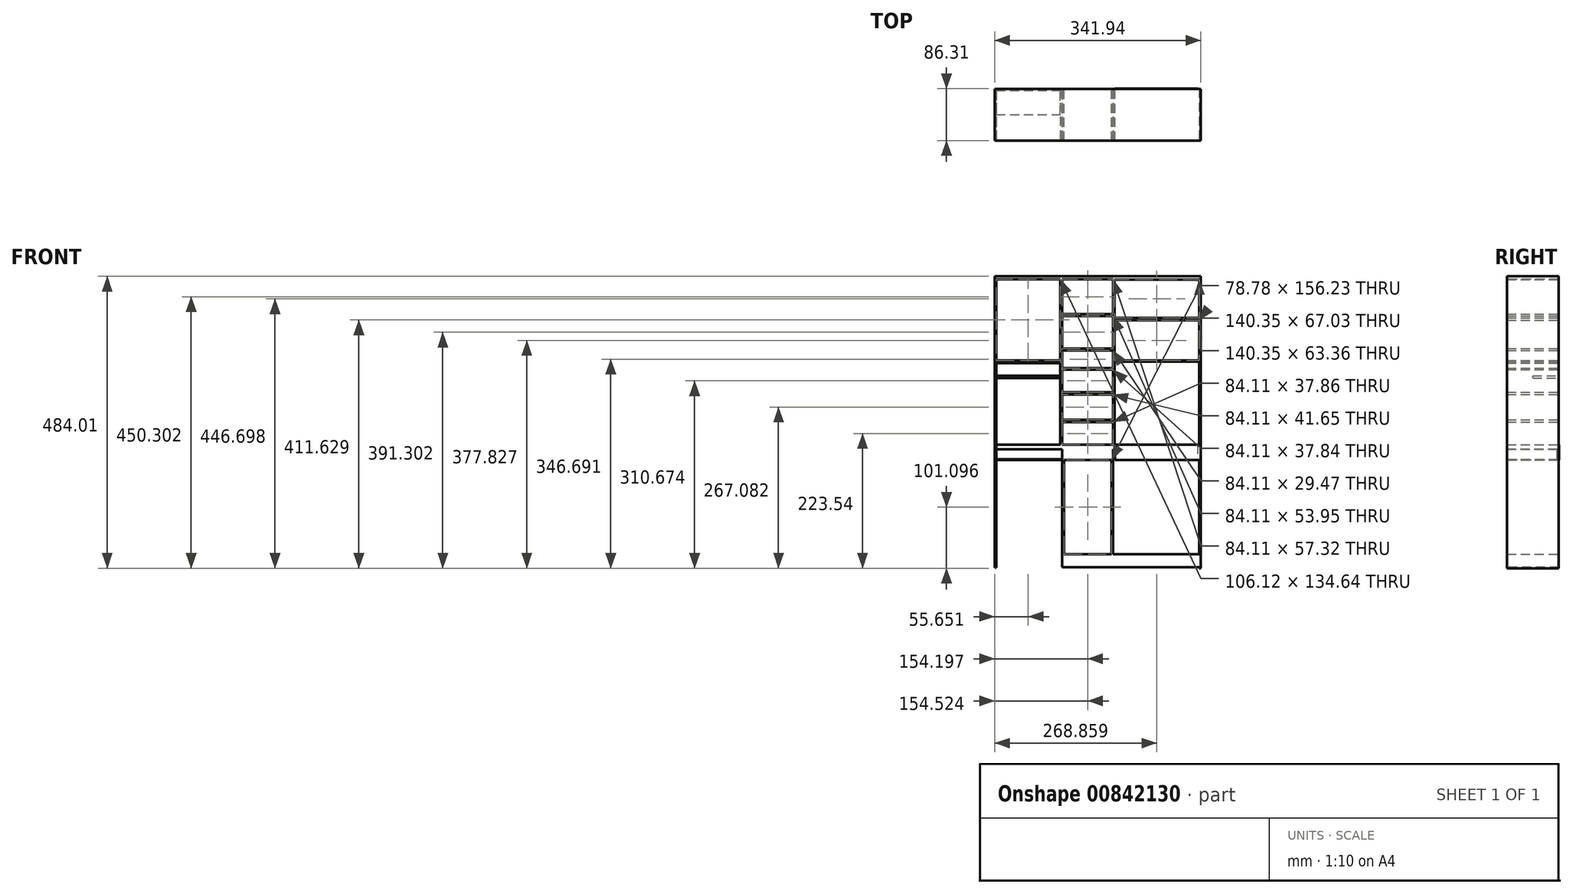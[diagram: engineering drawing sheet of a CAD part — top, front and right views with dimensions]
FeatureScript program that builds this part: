
annotation { "Feature Type Name" : "Feature", "Feature Type Description" : "" }
export const myFeature = defineFeature(function(context is Context, id is Id, definition is map)
    precondition{}
    {
        {
            var Q0;
            Q0=qCreatedBy(makeId("Top.planeOp"),FACE);
            var sketch = newSketch(context, id + "F0", { "sketchPlane" : qUnion([Q0])});
            skLineSegment(sketch, "E0.bottom", {"start": v(-181.1, 86) * mm, "end": v(155.92, 86) * mm});
            skLineSegment(sketch, "E0.top", {"start": v(-181.1, 0) * mm, "end": v(155.92, 0) * mm});
            skLineSegment(sketch, "E0.left", {"start": v(-181.1, 86) * mm, "end": v(-181.1, 0) * mm});
            skLineSegment(sketch, "E0.right", {"start": v(155.92, 86) * mm, "end": v(155.92, 0) * mm});
            skSolve(sketch);
        }
        {
            var Q0;
            Q0 = qSketchRegion(id + "F0", true);
            extrude(context, id + "F1", {"entities" : qUnion([Q0]), "depth" : 7.62 * mm, "offsetDistance" : 25.4 * mm});
        }
        {
            var Q0;
            Q0=makeQuery(id+"F1.opExtrude","CAP_FACE",FACE,{"disambiguationData":[OSD([sQuery(id+"F0.wireOp",EDGE,"E0.bottom"),sQuery(id+"F0.wireOp",EDGE,"E0.top"),sQuery(id+"F0.wireOp",EDGE,"E0.left"),sQuery(id+"F0.wireOp",EDGE,"E0.right")])],"isStart":false});
            var sketch = newSketch(context, id + "F2", { "sketchPlane" : qUnion([Q0])});
            skLineSegment(sketch, "E1.bottom", {"start": v(-75.06, 86) * mm, "end": v(-71.63, 86) * mm});
            skLineSegment(sketch, "E1.top", {"start": v(-75.06, 0) * mm, "end": v(-71.63, 0) * mm});
            skLineSegment(sketch, "E1.left", {"start": v(-75.06, 86) * mm, "end": v(-75.06, 0) * mm});
            skLineSegment(sketch, "E1.right", {"start": v(-71.63, 86) * mm, "end": v(-71.63, 0) * mm});
            skSolve(sketch);
        }
        {
            var Q0;
            Q0 = qSketchRegion(id + "F2", true);
            extrude(context, id + "F3", {"entities" : qUnion([Q0]), "operationType" : NewBodyOperationType.ADD, "depth" : 279.4 * mm, "offsetDistance" : 25.4 * mm});
        }
        {
            var Q0;
            Q0=makeQuery(id+"F3.opExtrude","SWEPT_FACE",FACE,{"disambiguationData":[OSD([sQuery(id+"F2.wireOp",EDGE,"E1.left")])]});
            var sketch = newSketch(context, id + "F4", { "sketchPlane" : qUnion([Q0])});
            skLineSegment(sketch, "E2.bottom", {"start": v(0, 147.32) * mm, "end": v(-86, 147.32) * mm});
            skLineSegment(sketch, "E2.top", {"start": v(0, 142.91) * mm, "end": v(-86, 142.91) * mm});
            skLineSegment(sketch, "E2.left", {"start": v(0, 147.32) * mm, "end": v(0, 142.91) * mm});
            skLineSegment(sketch, "E2.right", {"start": v(-86, 147.32) * mm, "end": v(-86, 142.91) * mm});
            skSolve(sketch);
        }
        {
            var Q0;
            Q0 = qSketchRegion(id + "F4", true);
            extrude(context, id + "F5", {"entities" : qUnion([Q0]), "operationType" : NewBodyOperationType.ADD, "depth" : 108.7 * mm, "offsetDistance" : 25.4 * mm});
        }
        {
            var Q0;
            Q0=makeQuery(id+"F5.boolean.opBoolean","SPLIT",FACE,{"disambiguationData":[TD([makeQuery(id+"F5.opExtrude","SWEPT_FACE",FACE,{"disambiguationData":[OSD([sQuery(id+"F4.wireOp",EDGE,"E2.top")])]})])],"derivedFrom":makeQuery(id+"F3.opExtrude","SWEPT_FACE",FACE,{"disambiguationData":[OSD([sQuery(id+"F2.wireOp",EDGE,"E1.left")])]})});
            var sketch = newSketch(context, id + "F6", { "sketchPlane" : qUnion([Q0])});
            skPoint(sketch, "E3.firstSnap0", {"position": v(-43, 142.91) * mm});
            skLineSegment(sketch, "E3.bottom", {"start": v(-43, 118.16) * mm, "end": v(-86, 118.16) * mm});
            skLineSegment(sketch, "E3.top", {"start": v(-43, 122.35) * mm, "end": v(-86, 122.35) * mm});
            skLineSegment(sketch, "E3.left", {"start": v(-43, 118.16) * mm, "end": v(-43, 122.35) * mm});
            skLineSegment(sketch, "E3.right", {"start": v(-86, 118.16) * mm, "end": v(-86, 122.35) * mm});
            skSolve(sketch);
        }
        {
            var Q0;
            Q0 = qSketchRegion(id + "F6", true);
            extrude(context, id + "F7", {"entities" : qUnion([Q0]), "operationType" : NewBodyOperationType.ADD, "depth" : 108.7 * mm, "offsetDistance" : 25.4 * mm});
        }
        {
            var Q0;
            {var subQ1=sQuery(id+"F2.wireOp",EDGE,"E1.left");Q0=makeQuery(id+"F5.boolean.opBoolean","SPLIT",FACE,{"disambiguationData":[TD([makeQuery(id+"F5.opExtrude","SWEPT_FACE",FACE,{"disambiguationData":[OSD([sQuery(id+"F4.wireOp",EDGE,"E2.bottom")])]})])],"derivedFrom":makeQuery(id+"F3.opExtrude","SWEPT_FACE",FACE,{"disambiguationData":[OSD([subQ1])]})});}
            var sketch = newSketch(context, id + "F8", { "sketchPlane" : qUnion([Q0])});
            skLineSegment(sketch, "E4.bottom", {"start": v(-86, 287.02) * mm, "end": v(0, 287.02) * mm});
            skLineSegment(sketch, "E4.top", {"start": v(-86, 281.96) * mm, "end": v(0, 281.96) * mm});
            skLineSegment(sketch, "E4.left", {"start": v(-86, 287.02) * mm, "end": v(-86, 281.96) * mm});
            skLineSegment(sketch, "E4.right", {"start": v(0, 287.02) * mm, "end": v(0, 281.96) * mm});
            skSolve(sketch);
        }
        {
            var Q0;
            Q0=makeQuery(id+"F8.imprint","IMPRINT",FACE,{"disambiguationData":[TD([[makeQuery(id+"F8.imprint","IMPRINT",EDGE,{"derivedFrom":sQuery(id+"F8.wireOp",EDGE,"E4.bottom")}),-1.0]])]});
            extrude(context, id + "F9", {"entities" : qUnion([Q0]), "operationType" : NewBodyOperationType.ADD, "depth" : 108.7 * mm, "offsetDistance" : 25.4 * mm});
        }
        {
            var Q0;
            Q0=makeQuery(id+"F9.opExtrude","SWEPT_FACE",FACE,{"disambiguationData":[OSD([sQuery(id+"F8.wireOp",EDGE,"E4.top")])]});
            var sketch = newSketch(context, id + "F10", { "sketchPlane" : qUnion([Q0])});
            skLineSegment(sketch, "E5.bottom", {"start": v(-183.77, -86) * mm, "end": v(-181.18, -86) * mm});
            skLineSegment(sketch, "E5.top", {"start": v(-183.77, 0) * mm, "end": v(-181.18, 0) * mm});
            skLineSegment(sketch, "E5.left", {"start": v(-183.77, -86) * mm, "end": v(-183.77, 0) * mm});
            skLineSegment(sketch, "E5.right", {"start": v(-181.18, -86) * mm, "end": v(-181.18, 0) * mm});
            skSolve(sketch);
        }
        {
            var Q0;
            Q0 = qSketchRegion(id + "F10", true);
            extrude(context, id + "F11", {"entities" : qUnion([Q0]), "operationType" : NewBodyOperationType.ADD, "depth" : 282.7 * mm, "offsetDistance" : 25.4 * mm});
        }
        {
            var Q0;
            {var subQ0=sQuery(id+"F0.wireOp",EDGE,"E0.top");var subQ1=sQuery(id+"F0.wireOp",EDGE,"E0.right");var subQ2=sQuery(id+"F0.wireOp",EDGE,"E0.bottom");Q0=makeQuery(id+"F3.boolean.opBoolean","SPLIT",FACE,{"disambiguationData":[TD([makeQuery(id+"F1.opExtrude","SWEPT_FACE",FACE,{"disambiguationData":[OSD([subQ1])]})])],"derivedFrom":makeQuery(id+"F1.opExtrude","CAP_FACE",FACE,{"disambiguationData":[OSD([subQ2,subQ0,sQuery(id+"F0.wireOp",EDGE,"E0.left"),subQ1])],"isStart":false})});}
            var sketch = newSketch(context, id + "F12", { "sketchPlane" : qUnion([Q0])});
            skLineSegment(sketch, "E6.bottom", {"start": v(-71.63, 86) * mm, "end": v(12.9, 86) * mm});
            skLineSegment(sketch, "E6.top", {"start": v(-71.63, 0) * mm, "end": v(12.9, 0) * mm});
            skLineSegment(sketch, "E6.left", {"start": v(-71.63, 86) * mm, "end": v(-71.63, 0) * mm});
            skLineSegment(sketch, "E6.right", {"start": v(12.9, 86) * mm, "end": v(12.9, 0) * mm});
            skSolve(sketch);
        }
        {
            var Q0;
            Q0 = qSketchRegion(id + "F12", true);
            extrude(context, id + "F13", {"entities" : qUnion([Q0]), "operationType" : NewBodyOperationType.ADD, "oppositeDirection" : true, "depth" : 25.4 * mm, "offsetDistance" : 25.4 * mm});
        }
        {
            var Q0;
            {var subQ0=sQuery(id+"F0.wireOp",EDGE,"E0.top");var subQ1=sQuery(id+"F0.wireOp",EDGE,"E0.right");var subQ2=sQuery(id+"F0.wireOp",EDGE,"E0.bottom");Q0=makeQuery(id+"F3.boolean.opBoolean","SPLIT",FACE,{"disambiguationData":[TD([makeQuery(id+"F1.opExtrude","SWEPT_FACE",FACE,{"disambiguationData":[OSD([subQ1])]})])],"derivedFrom":makeQuery(id+"F1.opExtrude","CAP_FACE",FACE,{"disambiguationData":[OSD([subQ2,subQ0,sQuery(id+"F0.wireOp",EDGE,"E0.left"),subQ1])],"isStart":false})});}
            var sketch = newSketch(context, id + "F14", { "sketchPlane" : qUnion([Q0])});
            skLineSegment(sketch, "E7.bottom", {"start": v(14.91, 0) * mm, "end": v(12.48, 0) * mm});
            skLineSegment(sketch, "E7.top", {"start": v(14.91, 86) * mm, "end": v(12.48, 86) * mm});
            skLineSegment(sketch, "E7.left", {"start": v(14.91, 0) * mm, "end": v(14.91, 86) * mm});
            skLineSegment(sketch, "E7.right", {"start": v(12.48, 0) * mm, "end": v(12.48, 86) * mm});
            skSolve(sketch);
        }
        {
            var Q0;
            Q0 = qSketchRegion(id + "F14", true);
            extrude(context, id + "F15", {"entities" : qUnion([Q0]), "operationType" : NewBodyOperationType.ADD, "depth" : 279.4 * mm, "offsetDistance" : 25.4 * mm});
        }
        {
            var Q0;
            Q0=makeQuery(id+"F3.opExtrude","SWEPT_FACE",FACE,{"disambiguationData":[OSD([sQuery(id+"F2.wireOp",EDGE,"E1.right")])]});
            var sketch = newSketch(context, id + "F16", { "sketchPlane" : qUnion([Q0])});
            skLineSegment(sketch, "E8.bottom", {"start": v(0, 287.02) * mm, "end": v(86, 287.02) * mm});
            skLineSegment(sketch, "E8.top", {"start": v(0, 281.97) * mm, "end": v(86, 281.97) * mm});
            skLineSegment(sketch, "E8.left", {"start": v(0, 287.02) * mm, "end": v(0, 281.97) * mm});
            skLineSegment(sketch, "E8.right", {"start": v(86, 287.02) * mm, "end": v(86, 281.97) * mm});
            skSolve(sketch);
        }
        {
            var Q0;
            Q0 = qSketchRegion(id + "F16", true);
            extrude(context, id + "F17", {"entities" : qUnion([Q0]), "operationType" : NewBodyOperationType.ADD, "depth" : 84.84 * mm, "offsetDistance" : 25.4 * mm});
        }
        {
            var Q0;
            Q0=makeQuery(id+"F3.opExtrude","SWEPT_FACE",FACE,{"disambiguationData":[OSD([sQuery(id+"F2.wireOp",EDGE,"E1.right")])]});
            var sketch = newSketch(context, id + "F18", { "sketchPlane" : qUnion([Q0])});
            skLineSegment(sketch, "E9.bottom", {"start": v(0, 164.43) * mm, "end": v(86, 164.43) * mm});
            skLineSegment(sketch, "E9.top", {"start": v(0, 167.33) * mm, "end": v(86, 167.33) * mm});
            skLineSegment(sketch, "E9.left", {"start": v(0, 164.43) * mm, "end": v(0, 167.33) * mm});
            skLineSegment(sketch, "E9.right", {"start": v(86, 164.43) * mm, "end": v(86, 167.33) * mm});
            skSolve(sketch);
        }
        {
            var Q0;
            Q0 = qSketchRegion(id + "F18", true);
            extrude(context, id + "F19", {"entities" : qUnion([Q0]), "operationType" : NewBodyOperationType.ADD, "depth" : 84.84 * mm, "offsetDistance" : 25.4 * mm});
        }
        {
            var Q0;
            Q0=makeQuery(id+"F19.boolean.opBoolean","SPLIT",FACE,{"disambiguationData":[TD([makeQuery(id+"F17.opExtrude","SWEPT_FACE",FACE,{"disambiguationData":[OSD([sQuery(id+"F16.wireOp",EDGE,"E8.top")])]})])],"derivedFrom":makeQuery(id+"F3.opExtrude","SWEPT_FACE",FACE,{"disambiguationData":[OSD([sQuery(id+"F2.wireOp",EDGE,"E1.right")])]})});
            var sketch = newSketch(context, id + "F20", { "sketchPlane" : qUnion([Q0])});
            skLineSegment(sketch, "E10.bottom", {"start": v(0, 224.65) * mm, "end": v(86, 224.65) * mm});
            skLineSegment(sketch, "E10.top", {"start": v(0, 221.29) * mm, "end": v(86, 221.29) * mm});
            skLineSegment(sketch, "E10.left", {"start": v(0, 224.65) * mm, "end": v(0, 221.29) * mm});
            skLineSegment(sketch, "E10.right", {"start": v(86, 224.65) * mm, "end": v(86, 221.29) * mm});
            skSolve(sketch);
        }
        {
            var Q0;
            Q0 = qSketchRegion(id + "F20", true);
            extrude(context, id + "F21", {"entities" : qUnion([Q0]), "operationType" : NewBodyOperationType.ADD, "depth" : 85.1 * mm, "offsetDistance" : 25.4 * mm});
        }
        {
            var Q0;
            Q0=makeQuery(id+"F19.boolean.opBoolean","SPLIT",FACE,{"disambiguationData":[TD([makeQuery(id+"F19.opExtrude","SWEPT_FACE",FACE,{"disambiguationData":[OSD([sQuery(id+"F18.wireOp",EDGE,"E9.bottom")])]})])],"derivedFrom":makeQuery(id+"F3.opExtrude","SWEPT_FACE",FACE,{"disambiguationData":[OSD([sQuery(id+"F2.wireOp",EDGE,"E1.right")])]})});
            var sketch = newSketch(context, id + "F22", { "sketchPlane" : qUnion([Q0])});
            skLineSegment(sketch, "E11.bottom", {"start": v(0, 132.6) * mm, "end": v(86, 132.6) * mm});
            skLineSegment(sketch, "E11.top", {"start": v(0, 134.97) * mm, "end": v(86, 134.97) * mm});
            skLineSegment(sketch, "E11.left", {"start": v(0, 132.6) * mm, "end": v(0, 134.97) * mm});
            skLineSegment(sketch, "E11.right", {"start": v(86, 132.6) * mm, "end": v(86, 134.97) * mm});
            skSolve(sketch);
        }
        {
            var Q0;
            Q0 = qSketchRegion(id + "F22", true);
            extrude(context, id + "F23", {"entities" : qUnion([Q0]), "operationType" : NewBodyOperationType.ADD, "depth" : 85.1 * mm, "offsetDistance" : 25.4 * mm});
        }
        {
            var Q0;
            Q0=makeQuery(id+"F23.boolean.opBoolean","SPLIT",FACE,{"disambiguationData":[TD([makeQuery(id+"F23.opExtrude","SWEPT_FACE",FACE,{"disambiguationData":[OSD([sQuery(id+"F22.wireOp",EDGE,"E11.bottom")])]})])],"derivedFrom":makeQuery(id+"F19.boolean.opBoolean","SPLIT",FACE,{"disambiguationData":[TD([makeQuery(id+"F19.opExtrude","SWEPT_FACE",FACE,{"disambiguationData":[OSD([sQuery(id+"F18.wireOp",EDGE,"E9.bottom")])]})])],"derivedFrom":makeQuery(id+"F3.opExtrude","SWEPT_FACE",FACE,{"disambiguationData":[OSD([sQuery(id+"F2.wireOp",EDGE,"E1.right")])]})})});
            var sketch = newSketch(context, id + "F24", { "sketchPlane" : qUnion([Q0])});
            skLineSegment(sketch, "E12.bottom", {"start": v(0, 94.76) * mm, "end": v(86, 94.76) * mm});
            skLineSegment(sketch, "E12.top", {"start": v(0, 90.92) * mm, "end": v(86, 90.92) * mm});
            skLineSegment(sketch, "E12.left", {"start": v(0, 94.76) * mm, "end": v(0, 90.92) * mm});
            skLineSegment(sketch, "E12.right", {"start": v(86, 94.76) * mm, "end": v(86, 90.92) * mm});
            skSolve(sketch);
        }
        {
            var Q0;
            Q0 = qSketchRegion(id + "F24", true);
            extrude(context, id + "F25", {"entities" : qUnion([Q0]), "operationType" : NewBodyOperationType.ADD, "depth" : 85.1 * mm, "offsetDistance" : 25.4 * mm});
        }
        {
            var Q0;
            Q0=makeQuery(id+"F25.boolean.opBoolean","SPLIT",FACE,{"disambiguationData":[TD([makeQuery(id+"F25.opExtrude","SWEPT_FACE",FACE,{"disambiguationData":[OSD([sQuery(id+"F24.wireOp",EDGE,"E12.top")])]})])],"derivedFrom":makeQuery(id+"F23.boolean.opBoolean","SPLIT",FACE,{"disambiguationData":[TD([makeQuery(id+"F23.opExtrude","SWEPT_FACE",FACE,{"disambiguationData":[OSD([sQuery(id+"F22.wireOp",EDGE,"E11.bottom")])]})])],"derivedFrom":makeQuery(id+"F19.boolean.opBoolean","SPLIT",FACE,{"disambiguationData":[TD([makeQuery(id+"F19.opExtrude","SWEPT_FACE",FACE,{"disambiguationData":[OSD([sQuery(id+"F18.wireOp",EDGE,"E9.bottom")])]})])],"derivedFrom":makeQuery(id+"F3.opExtrude","SWEPT_FACE",FACE,{"disambiguationData":[OSD([sQuery(id+"F2.wireOp",EDGE,"E1.right")])]})})})});
            var sketch = newSketch(context, id + "F26", { "sketchPlane" : qUnion([Q0])});
            skLineSegment(sketch, "E13.bottom", {"start": v(0, 49.27) * mm, "end": v(86, 49.27) * mm});
            skLineSegment(sketch, "E13.top", {"start": v(0, 45.48) * mm, "end": v(86, 45.48) * mm});
            skLineSegment(sketch, "E13.left", {"start": v(0, 49.27) * mm, "end": v(0, 45.48) * mm});
            skLineSegment(sketch, "E13.right", {"start": v(86, 49.27) * mm, "end": v(86, 45.48) * mm});
            skSolve(sketch);
        }
        {
            var Q0;
            Q0 = qSketchRegion(id + "F26", true);
            extrude(context, id + "F27", {"entities" : qUnion([Q0]), "operationType" : NewBodyOperationType.ADD, "depth" : 85.1 * mm, "offsetDistance" : 25.4 * mm});
        }
        {
            var Q0;
            {var subQ1=sQuery(id+"F0.wireOp",EDGE,"E0.bottom");var subQ3=sQuery(id+"F0.wireOp",EDGE,"E0.right");var subQ4=makeQuery(id+"F1.opExtrude","SWEPT_FACE",FACE,{"disambiguationData":[OSD([subQ3])]});var subQ5=sQuery(id+"F0.wireOp",EDGE,"E0.top");Q0=makeQuery(id+"F15.boolean.opBoolean","SPLIT",FACE,{"disambiguationData":[TD([subQ4])],"derivedFrom":makeQuery(id+"F3.boolean.opBoolean","SPLIT",FACE,{"disambiguationData":[TD([subQ4])],"derivedFrom":makeQuery(id+"F1.opExtrude","CAP_FACE",FACE,{"disambiguationData":[OSD([subQ1,subQ5,sQuery(id+"F0.wireOp",EDGE,"E0.left"),subQ3])],"isStart":false})})});}
            var sketch = newSketch(context, id + "F28", { "sketchPlane" : qUnion([Q0])});
            skSolve(sketch);
        }
        {
            var Q0;
            {var subQ0=sQuery(id+"F0.wireOp",EDGE,"E0.right");Q0=makeQuery(id+"F28.imprint","IMPRINT",FACE,{"disambiguationData":[TD([[makeQuery(id+"F28.imprint","IMPRINT",EDGE,{"derivedFrom":makeQuery(id+"F1.opExtrude","CAP_EDGE",EDGE,{"disambiguationData":[OSD([subQ0])],"isStart":false})}),-1.0]])]});}
            var sketch = newSketch(context, id + "F29", { "sketchPlane" : qUnion([Q0])});
            skLineSegment(sketch, "E14.bottom", {"start": v(15.66, 0) * mm, "end": v(153.22, 0) * mm});
            skLineSegment(sketch, "E14.top", {"start": v(15.66, 86.3) * mm, "end": v(153.22, 86.3) * mm});
            skLineSegment(sketch, "E14.left", {"start": v(15.66, 0) * mm, "end": v(15.66, 86.3) * mm});
            skLineSegment(sketch, "E14.right", {"start": v(153.22, 0) * mm, "end": v(153.22, 86.3) * mm});
            skSolve(sketch);
        }
        {
            var Q0;
            Q0 = qSketchRegion(id + "F29", true);
            extrude(context, id + "F30", {"entities" : qUnion([Q0]), "operationType" : NewBodyOperationType.ADD, "oppositeDirection" : true, "depth" : 25.4 * mm, "offsetDistance" : 25.4 * mm});
        }
        {
            var Q0;
            Q0=makeQuery(id+"F15.opExtrude","SWEPT_FACE",FACE,{"disambiguationData":[OSD([sQuery(id+"F14.wireOp",EDGE,"E7.left")])]});
            var sketch = newSketch(context, id + "F31", { "sketchPlane" : qUnion([Q0])});
            skLineSegment(sketch, "E15.bottom", {"start": v(0, 147.32) * mm, "end": v(86, 147.32) * mm});
            skLineSegment(sketch, "E15.top", {"start": v(0, 145.59) * mm, "end": v(86, 145.59) * mm});
            skLineSegment(sketch, "E15.left", {"start": v(0, 147.32) * mm, "end": v(0, 145.59) * mm});
            skLineSegment(sketch, "E15.right", {"start": v(86, 147.32) * mm, "end": v(86, 145.59) * mm});
            skSolve(sketch);
        }
        {
            var Q0;
            Q0 = qSketchRegion(id + "F31", true);
            extrude(context, id + "F32", {"entities" : qUnion([Q0]), "operationType" : NewBodyOperationType.ADD, "depth" : 143.26 * mm, "offsetDistance" : 25.4 * mm});
        }
        {
            var Q0;
            {var subQ2=sQuery(id+"F14.wireOp",EDGE,"E7.left");Q0=makeQuery(id+"F32.boolean.opBoolean","SPLIT",FACE,{"disambiguationData":[TD([makeQuery(id+"F9.opExtrude","SWEPT_FACE",FACE,{"disambiguationData":[OSD([sQuery(id+"F8.wireOp",EDGE,"E4.bottom")])]})])],"derivedFrom":makeQuery(id+"F15.opExtrude","SWEPT_FACE",FACE,{"disambiguationData":[OSD([subQ2])]})});}
            var sketch = newSketch(context, id + "F33", { "sketchPlane" : qUnion([Q0])});
            skLineSegment(sketch, "E16.bottom", {"start": v(0, 287.02) * mm, "end": v(86, 287.02) * mm});
            skLineSegment(sketch, "E16.top", {"start": v(0, 281.39) * mm, "end": v(86, 281.39) * mm});
            skLineSegment(sketch, "E16.left", {"start": v(0, 287.02) * mm, "end": v(0, 281.39) * mm});
            skLineSegment(sketch, "E16.right", {"start": v(86, 287.02) * mm, "end": v(86, 281.39) * mm});
            skSolve(sketch);
        }
        {
            var Q0;
            Q0=makeQuery(id+"F33.imprint","IMPRINT",FACE,{"disambiguationData":[TD([[makeQuery(id+"F33.imprint","IMPRINT",EDGE,{"derivedFrom":sQuery(id+"F33.wireOp",EDGE,"E16.bottom")}),-1.0]])]});
            extrude(context, id + "F34", {"entities" : qUnion([Q0]), "operationType" : NewBodyOperationType.ADD, "depth" : 143.26 * mm, "offsetDistance" : 25.4 * mm});
        }
        {
            var Q0;
            Q0=makeQuery(id+"F34.opExtrude","SWEPT_FACE",FACE,{"disambiguationData":[OSD([sQuery(id+"F33.wireOp",EDGE,"E16.top")])]});
            var sketch = newSketch(context, id + "F35", { "sketchPlane" : qUnion([Q0])});
            skLineSegment(sketch, "E17.bottom", {"start": v(158.17, 0) * mm, "end": v(155.27, 0) * mm});
            skLineSegment(sketch, "E17.top", {"start": v(158.17, -86) * mm, "end": v(155.27, -86) * mm});
            skLineSegment(sketch, "E17.left", {"start": v(158.17, 0) * mm, "end": v(158.17, -86) * mm});
            skLineSegment(sketch, "E17.right", {"start": v(155.27, 0) * mm, "end": v(155.27, -86) * mm});
            skSolve(sketch);
        }
        {
            var Q0;
            Q0 = qSketchRegion(id + "F35", true);
            extrude(context, id + "F36", {"entities" : qUnion([Q0]), "operationType" : NewBodyOperationType.ADD, "depth" : 300.58 * mm, "offsetDistance" : 25.4 * mm});
        }
        {
            var Q0;
            {var subQ2=sQuery(id+"F14.wireOp",EDGE,"E7.left");Q0=makeQuery(id+"F32.boolean.opBoolean","SPLIT",FACE,{"disambiguationData":[TD([makeQuery(id+"F9.opExtrude","SWEPT_FACE",FACE,{"disambiguationData":[OSD([sQuery(id+"F8.wireOp",EDGE,"E4.bottom")])]})])],"derivedFrom":makeQuery(id+"F15.opExtrude","SWEPT_FACE",FACE,{"disambiguationData":[OSD([subQ2])]})});}
            var sketch = newSketch(context, id + "F37", { "sketchPlane" : qUnion([Q0])});
            skLineSegment(sketch, "E18.bottom", {"start": v(0, 214.35) * mm, "end": v(86, 214.35) * mm});
            skLineSegment(sketch, "E18.top", {"start": v(0, 218.03) * mm, "end": v(86, 218.03) * mm});
            skLineSegment(sketch, "E18.left", {"start": v(0, 214.35) * mm, "end": v(0, 218.03) * mm});
            skLineSegment(sketch, "E18.right", {"start": v(86, 214.35) * mm, "end": v(86, 218.03) * mm});
            skSolve(sketch);
        }
        {
            var Q0;
            Q0 = qSketchRegion(id + "F37", true);
            extrude(context, id + "F38", {"entities" : qUnion([Q0]), "operationType" : NewBodyOperationType.ADD, "depth" : 141.73 * mm, "offsetDistance" : 25.4 * mm});
        }
        {
            var Q0;
            {var subQ0=sQuery(id+"F0.wireOp",EDGE,"E0.bottom");var subQ1=sQuery(id+"F0.wireOp",EDGE,"E0.top");var subQ2=sQuery(id+"F0.wireOp",EDGE,"E0.left");Q0=makeQuery(id+"F13.boolean.opBoolean","SPLIT",FACE,{"disambiguationData":[TD([makeQuery(id+"F1.opExtrude","SWEPT_FACE",FACE,{"disambiguationData":[OSD([subQ2])]})])],"derivedFrom":makeQuery(id+"F1.opExtrude","CAP_FACE",FACE,{"disambiguationData":[OSD([subQ0,subQ1,subQ2,sQuery(id+"F0.wireOp",EDGE,"E0.right")])],"isStart":true})});}
            var sketch = newSketch(context, id + "F39", { "sketchPlane" : qUnion([Q0])});
            skLineSegment(sketch, "E19.bottom", {"start": v(-181.1, -86) * mm, "end": v(-71.63, -86) * mm});
            skLineSegment(sketch, "E19.top", {"start": v(-181.1, -83.2) * mm, "end": v(-71.63, -83.2) * mm});
            skLineSegment(sketch, "E19.left", {"start": v(-181.1, -86) * mm, "end": v(-181.1, -83.2) * mm});
            skLineSegment(sketch, "E19.right", {"start": v(-71.63, -86) * mm, "end": v(-71.63, -83.2) * mm});
            skSolve(sketch);
        }
        {
            var Q0;
            Q0 = qSketchRegion(id + "F39", true);
            extrude(context, id + "F40", {"entities" : qUnion([Q0]), "operationType" : NewBodyOperationType.ADD, "depth" : 17.78 * mm, "offsetDistance" : 25.4 * mm});
        }
        {
            var Q0;
            Q0=makeQuery(id+"F11.opExtrude","CAP_FACE",FACE,{"disambiguationData":[OSD([sQuery(id+"F10.wireOp",EDGE,"E5.bottom"),sQuery(id+"F10.wireOp",EDGE,"E5.top"),sQuery(id+"F10.wireOp",EDGE,"E5.left"),sQuery(id+"F10.wireOp",EDGE,"E5.right")])],"isStart":false});
            var sketch = newSketch(context, id + "F41", { "sketchPlane" : qUnion([Q0])});
            skLineSegment(sketch, "E20.bottom", {"start": v(-181.18, -86) * mm, "end": v(-183.77, -86) * mm});
            skLineSegment(sketch, "E20.top", {"start": v(-181.18, -83.2) * mm, "end": v(-183.77, -83.2) * mm});
            skLineSegment(sketch, "E20.left", {"start": v(-181.18, -86) * mm, "end": v(-181.18, -83.2) * mm});
            skLineSegment(sketch, "E20.right", {"start": v(-183.77, -86) * mm, "end": v(-183.77, -83.2) * mm});
            skSolve(sketch);
        }
        {
            var Q0;
            Q0 = qSketchRegion(id + "F41", true);
            extrude(context, id + "F42", {"entities" : qUnion([Q0]), "operationType" : NewBodyOperationType.ADD, "depth" : 17.07 * mm, "offsetDistance" : 25.4 * mm});
        }
        {
            var Q0;
            Q0=makeQuery(id+"F42.opExtrude","SWEPT_FACE",FACE,{"disambiguationData":[OSD([sQuery(id+"F41.wireOp",EDGE,"E20.top")])]});
            extrude(context, id + "F43", {"entities" : qUnion([Q0]), "operationType" : NewBodyOperationType.ADD, "depth" : 83.16 * mm, "offsetDistance" : 25.4 * mm});
        }
        {
            var Q0;
            Q0=makeQuery(id+"F40.opExtrude","SWEPT_FACE",FACE,{"disambiguationData":[OSD([sQuery(id+"F39.wireOp",EDGE,"E19.top")])]});
            var sketch = newSketch(context, id + "F44", { "sketchPlane" : qUnion([Q0])});
            skLineSegment(sketch, "E21.bottom", {"start": v(-71.63, -16.3) * mm, "end": v(-181.1, -16.3) * mm});
            skLineSegment(sketch, "E21.top", {"start": v(-71.63, -17.78) * mm, "end": v(-181.1, -17.78) * mm});
            skLineSegment(sketch, "E21.left", {"start": v(-71.63, -16.3) * mm, "end": v(-71.63, -17.78) * mm});
            skLineSegment(sketch, "E21.right", {"start": v(-181.1, -16.3) * mm, "end": v(-181.1, -17.78) * mm});
            skSolve(sketch);
        }
        {
            var Q0;
            Q0 = qSketchRegion(id + "F44", true);
            extrude(context, id + "F45", {"entities" : qUnion([Q0]), "operationType" : NewBodyOperationType.ADD, "depth" : 83.06 * mm, "offsetDistance" : 25.4 * mm});
        }
        {
            var Q0;
            {var subQ0=sQuery(id+"F41.wireOp",EDGE,"E20.top");Q0=makeQuery(id+"F43.boolean.opBoolean","MERGE",FACE,{"derivedFrom":[makeQuery(id+"F42.opExtrude","CAP_FACE",FACE,{"disambiguationData":[OSD([sQuery(id+"F41.wireOp",EDGE,"E20.bottom"),subQ0,sQuery(id+"F41.wireOp",EDGE,"E20.left"),sQuery(id+"F41.wireOp",EDGE,"E20.right")])],"isStart":false}),makeQuery(id+"F43.opExtrude","SWEPT_FACE",FACE,{"disambiguationData":[OSD([subQ0]),TDD([makeQuery(id+"F42.opExtrude","CAP_EDGE",EDGE,{"disambiguationData":[OSD([subQ0])],"isStart":false})])]})]});}
            extrude(context, id + "F46", {"entities" : qUnion([Q0]), "operationType" : NewBodyOperationType.ADD, "depth" : 177.8 * mm, "offsetDistance" : 25.4 * mm});
        }
        {
            var Q0;
            Q0=makeQuery(id+"F45.boolean.opBoolean","MERGE",FACE,{"derivedFrom":[makeQuery(id+"F40.boolean.opBoolean","MERGE",FACE,{"derivedFrom":[makeQuery(id+"F13.opExtrude","CAP_FACE",FACE,{"disambiguationData":[OSD([sQuery(id+"F12.wireOp",EDGE,"E6.bottom"),sQuery(id+"F12.wireOp",EDGE,"E6.top"),sQuery(id+"F12.wireOp",EDGE,"E6.left"),sQuery(id+"F12.wireOp",EDGE,"E6.right")])],"isStart":false}),makeQuery(id+"F40.opExtrude","CAP_FACE",FACE,{"disambiguationData":[OSD([sQuery(id+"F39.wireOp",EDGE,"E19.bottom"),sQuery(id+"F39.wireOp",EDGE,"E19.top"),sQuery(id+"F39.wireOp",EDGE,"E19.left"),sQuery(id+"F39.wireOp",EDGE,"E19.right")])],"isStart":false})]}),makeQuery(id+"F45.opExtrude","SWEPT_FACE",FACE,{"disambiguationData":[OSD([sQuery(id+"F44.wireOp",EDGE,"E21.top")])]})]});
            var sketch = newSketch(context, id + "F47", { "sketchPlane" : qUnion([Q0])});
            skLineSegment(sketch, "E22.bottom", {"start": v(-71.63, 0) * mm, "end": v(-68.64, 0) * mm});
            skLineSegment(sketch, "E22.top", {"start": v(-71.63, -86) * mm, "end": v(-68.64, -86) * mm});
            skLineSegment(sketch, "E22.left", {"start": v(-71.63, 0) * mm, "end": v(-71.63, -86) * mm});
            skLineSegment(sketch, "E22.right", {"start": v(-68.64, 0) * mm, "end": v(-68.64, -86) * mm});
            skSolve(sketch);
        }
        {
            var Q0;
            Q0 = qSketchRegion(id + "F47", true);
            extrude(context, id + "F48", {"entities" : qUnion([Q0]), "operationType" : NewBodyOperationType.ADD, "depth" : 177.8 * mm, "offsetDistance" : 25.4 * mm});
        }
        {
            var Q0;
            {var subQ0=sQuery(id+"F12.wireOp",EDGE,"E6.right");var subQ2=sQuery(id+"F12.wireOp",EDGE,"E6.top");var subQ3=sQuery(id+"F12.wireOp",EDGE,"E6.bottom");var subQ4=sQuery(id+"F39.wireOp",EDGE,"E19.bottom");Q0=makeQuery(id+"F48.boolean.opBoolean","SPLIT",FACE,{"disambiguationData":[TD([makeQuery(id+"F1.opExtrude","SWEPT_FACE",FACE,{"disambiguationData":[OSD([sQuery(id+"F0.wireOp",EDGE,"E0.top")])]})])],"derivedFrom":makeQuery(id+"F45.boolean.opBoolean","MERGE",FACE,{"derivedFrom":[makeQuery(id+"F40.boolean.opBoolean","MERGE",FACE,{"derivedFrom":[makeQuery(id+"F13.opExtrude","CAP_FACE",FACE,{"disambiguationData":[OSD([subQ3,subQ2,sQuery(id+"F12.wireOp",EDGE,"E6.left"),subQ0])],"isStart":false}),makeQuery(id+"F40.opExtrude","CAP_FACE",FACE,{"disambiguationData":[OSD([subQ4,sQuery(id+"F39.wireOp",EDGE,"E19.top"),sQuery(id+"F39.wireOp",EDGE,"E19.left"),sQuery(id+"F39.wireOp",EDGE,"E19.right")])],"isStart":false})]}),makeQuery(id+"F45.opExtrude","SWEPT_FACE",FACE,{"disambiguationData":[OSD([sQuery(id+"F44.wireOp",EDGE,"E21.top")])]})]})});}
            var sketch = newSketch(context, id + "F49", { "sketchPlane" : qUnion([Q0])});
            skLineSegment(sketch, "E23.bottom", {"start": v(12.9, 0) * mm, "end": v(10.14, 0) * mm});
            skLineSegment(sketch, "E23.top", {"start": v(12.9, -86) * mm, "end": v(10.14, -86) * mm});
            skLineSegment(sketch, "E23.left", {"start": v(12.9, 0) * mm, "end": v(12.9, -86) * mm});
            skLineSegment(sketch, "E23.right", {"start": v(10.14, 0) * mm, "end": v(10.14, -86) * mm});
            skSolve(sketch);
        }
        {
            var Q0;
            Q0 = qSketchRegion(id + "F49", true);
            extrude(context, id + "F50", {"entities" : qUnion([Q0]), "operationType" : NewBodyOperationType.ADD, "depth" : 177.8 * mm, "offsetDistance" : 25.4 * mm});
        }
        {
            var Q0;
            {var subQ4=sQuery(id+"F0.wireOp",EDGE,"E0.right");var subQ5=makeQuery(id+"F1.opExtrude","SWEPT_FACE",FACE,{"disambiguationData":[OSD([subQ4])]});var subQ7=sQuery(id+"F0.wireOp",EDGE,"E0.top");var subQ12=sQuery(id+"F0.wireOp",EDGE,"E0.bottom");Q0=makeQuery(id+"F30.boolean.opBoolean","SPLIT",FACE,{"disambiguationData":[TD([subQ5])],"derivedFrom":makeQuery(id+"F13.boolean.opBoolean","SPLIT",FACE,{"disambiguationData":[TD([subQ5])],"derivedFrom":makeQuery(id+"F1.opExtrude","CAP_FACE",FACE,{"disambiguationData":[OSD([subQ12,subQ7,sQuery(id+"F0.wireOp",EDGE,"E0.left"),subQ4])],"isStart":true})})});}
            extrude(context, id + "F51", {"entities" : qUnion([Q0]), "operationType" : NewBodyOperationType.ADD, "depth" : 17.78 * mm, "offsetDistance" : 25.4 * mm});
        }
        {
            var Q0;
            Q0=makeQuery(id+"F36.opExtrude","CAP_FACE",FACE,{"disambiguationData":[OSD([sQuery(id+"F35.wireOp",EDGE,"E17.bottom"),sQuery(id+"F35.wireOp",EDGE,"E17.top"),sQuery(id+"F35.wireOp",EDGE,"E17.left"),sQuery(id+"F35.wireOp",EDGE,"E17.right")])],"isStart":false});
            var sketch = newSketch(context, id + "F52", { "sketchPlane" : qUnion([Q0])});
            skSolve(sketch);
        }
        {
            var Q0;
            Q0 = qSketchRegion(id + "F52", true);
            var Q1;
            Q1=makeQuery(id+"F52.imprint","IMPRINT",FACE,{"disambiguationData":[TD([[makeQuery(id+"F52.imprint","IMPRINT",EDGE,{"derivedFrom":makeQuery(id+"F36.opExtrude","CAP_EDGE",EDGE,{"disambiguationData":[OSD([sQuery(id+"F35.wireOp",EDGE,"E17.bottom")])],"isStart":false})}),1.0]])]});
            extrude(context, id + "F53", {"entities" : qUnion([Q0, Q1]), "operationType" : NewBodyOperationType.ADD, "depth" : 177.8 * mm, "offsetDistance" : 25.4 * mm});
        }
        {
            var Q0;
            Q0=makeQuery(id+"F48.opExtrude","SWEPT_FACE",FACE,{"disambiguationData":[OSD([sQuery(id+"F47.wireOp",EDGE,"E22.right")])]});
            var sketch = newSketch(context, id + "F54", { "sketchPlane" : qUnion([Q0])});
            skLineSegment(sketch, "E24.bottom", {"start": v(0, -195.58) * mm, "end": v(86, -195.58) * mm});
            skLineSegment(sketch, "E24.top", {"start": v(0, -174) * mm, "end": v(86, -174) * mm});
            skLineSegment(sketch, "E24.left", {"start": v(0, -195.58) * mm, "end": v(0, -174) * mm});
            skLineSegment(sketch, "E24.right", {"start": v(86, -195.58) * mm, "end": v(86, -174) * mm});
            skSolve(sketch);
        }
        {
            var Q0;
            Q0 = qSketchRegion(id + "F54", true);
            extrude(context, id + "F55", {"entities" : qUnion([Q0]), "operationType" : NewBodyOperationType.ADD, "depth" : 226.06 * mm, "offsetDistance" : 25.4 * mm});
        }
    });
